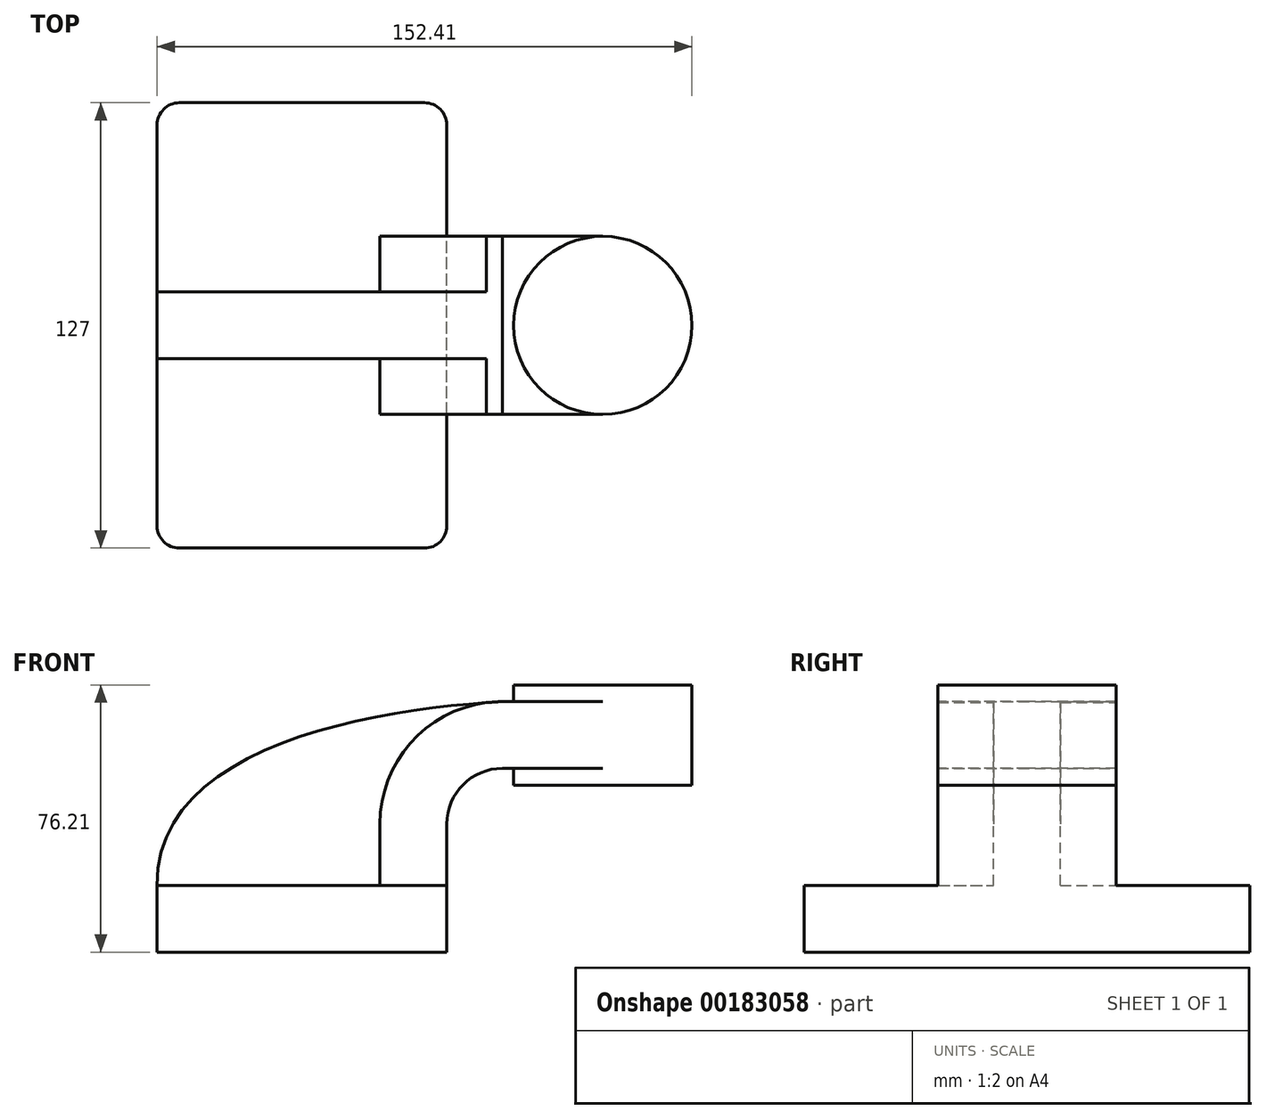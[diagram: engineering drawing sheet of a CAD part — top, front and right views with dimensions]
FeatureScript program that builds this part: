
annotation { "Feature Type Name" : "Feature", "Feature Type Description" : "" }
export const myFeature = defineFeature(function(context is Context, id is Id, definition is map)
    precondition{}
    {
        {
            var Q0;
            Q0=qCreatedBy(makeId("Front.planeOp"),FACE);
            var sketch = newSketch(context, id + "F0", { "sketchPlane" : qUnion([Q0])});
            skLineSegment(sketch, "E0.bottom", {"start": v(-41.28, -9.53) * mm, "end": v(41.28, -9.53) * mm});
            skLineSegment(sketch, "E0.top", {"start": v(-41.28, 9.53) * mm, "end": v(41.28, 9.53) * mm});
            skLineSegment(sketch, "E0.left", {"start": v(-41.28, -9.53) * mm, "end": v(-41.28, 9.53) * mm});
            skLineSegment(sketch, "E0.right", {"start": v(41.28, -9.53) * mm, "end": v(41.28, 9.53) * mm});
            skPoint(sketch, "E0.middle", {"position": v(0, 0) * mm});
            skLineSegment(sketch, "E1.bottom", {"start": v(60.32, 38.1) * mm, "end": v(111.12, 38.1) * mm});
            skLineSegment(sketch, "E1.top", {"start": v(60.32, 66.68) * mm, "end": v(111.12, 66.68) * mm});
            skLineSegment(sketch, "E1.left", {"start": v(60.32, 38.1) * mm, "end": v(60.32, 66.68) * mm});
            skLineSegment(sketch, "E1.right", {"start": v(111.12, 38.1) * mm, "end": v(111.12, 66.68) * mm});
            skPoint(sketch, "E1.middle", {"position": v(85.72, 52.39) * mm});
            skLineSegment(sketch, "E2", {"start": v(41.27, 9.53) * mm, "end": v(41.27, 27) * mm});
            skArc(sketch, "E3", {"start": v(41.27, 27) * mm, "mid": v(45.92, 38.23) * mm, "end": v(57.15, 42.88) * mm});
            skLineSegment(sketch, "E4", {"start": v(57.15, 42.88) * mm, "end": v(85.72, 42.88) * mm});
            skLineSegment(sketch, "E5.0", {"start": v(57.15, 61.93) * mm, "end": v(85.72, 61.93) * mm});
            skArc(sketch, "E5.1", {"start": v(22.22, 27) * mm, "mid": v(32.45, 51.7) * mm, "end": v(57.15, 61.93) * mm});
            skLineSegment(sketch, "E5.2", {"start": v(22.22, 9.53) * mm, "end": v(22.22, 27) * mm});
            skLineSegment(sketch, "E6", {"start": v(85.72, 38.1) * mm, "end": v(85.72, 66.68) * mm});
            skFitSpline(sketch, "E7", {"points": [v(-41.28, 9.52) * mm, v(57.15, 61.93) * mm], "startDerivative": vector(-1.05, 120.28) * mm, "endDerivative": vector(109.9, 6.42) * mm});
            skSolve(sketch);
        }
        {
            var Q0;
            Q0=makeQuery(id+"F0.imprint","IMPRINT",FACE,{"disambiguationData":[TD([[makeQuery(id+"F0.imprint","IMPRINT",EDGE,{"derivedFrom":sQuery(id+"F0.wireOp",EDGE,"E0.bottom")}),1.0]])]});
            extrude(context, id + "F1", {"entities" : qUnion([Q0]), "endBound" : BoundingType.SYMMETRIC, "depth" : 127 * mm});
        }
        {
            var Q0;
            {var subQ1=sQuery(id+"F0.wireOp",EDGE,"E2");Q0=makeQuery(id+"F0.imprint","IMPRINT",FACE,{"disambiguationData":[TD([[makeQuery(id+"F0.imprint","IMPRINT",EDGE,{"derivedFrom":subQ1}),1.0]])]});}
            extrude(context, id + "F2", {"entities" : qUnion([Q0]), "operationType" : NewBodyOperationType.ADD, "endBound" : BoundingType.SYMMETRIC, "depth" : 50.8 * mm});
        }
        {
            var Q0;
            {var subQ0=sQuery(id+"F0.wireOp",EDGE,"E4");var subQ1=sQuery(id+"F0.wireOp",EDGE,"E1.left");var subQ2=makeQuery(id+"F0.imprint","INTERSECT",VERTEX,{"derivedFrom":[subQ1,subQ0]});Q0=makeQuery(id+"F0.imprint","IMPRINT",FACE,{"disambiguationData":[TD([[makeQuery(id+"F0.imprint","IMPRINT",EDGE,{"disambiguationData":[TD([[subQ2,-1.0]])],"derivedFrom":subQ1}),-1.0]])]});}
            extrude(context, id + "F3", {"entities" : qUnion([Q0]), "operationType" : NewBodyOperationType.ADD, "endBound" : BoundingType.SYMMETRIC, "depth" : 50.8 * mm});
        }
        {
            var Q0;
            {var subQ3=sQuery(id+"F0.wireOp",EDGE,"E5.2");Q0=makeQuery(id+"F0.imprint","IMPRINT",FACE,{"disambiguationData":[TD([[makeQuery(id+"F0.imprint","IMPRINT",EDGE,{"derivedFrom":subQ3}),1.0]])]});}
            extrude(context, id + "F4", {"entities" : qUnion([Q0]), "operationType" : NewBodyOperationType.ADD, "endBound" : BoundingType.SYMMETRIC, "depth" : 19.05 * mm});
        }
        {
            var Q0;
            {var subQ0=sQuery(id+"F0.wireOp",EDGE,"E1.right");Q0=makeQuery(id+"F0.imprint","IMPRINT",FACE,{"disambiguationData":[TD([[makeQuery(id+"F0.imprint","IMPRINT",EDGE,{"derivedFrom":subQ0}),1.0]])]});}
            var Q1;
            Q1=sQuery(id+"F0.wireOp",EDGE,"E6");
            revolve(context, id + "F5", {"operationType" : NewBodyOperationType.ADD, "entities" : qUnion([Q0]), "axis" : qUnion([Q1]), "revolveType" : RevolveType.FULL});
        }
        {
            var Q0;
            Q0=makeQuery(id+"F1.opExtrude","CAP_EDGE",EDGE,{"disambiguationData":[OSD([sQuery(id+"F0.wireOp",EDGE,"E0.left")])],"isStart":false});
            var Q1;
            Q1=makeQuery(id+"F1.opExtrude","CAP_EDGE",EDGE,{"disambiguationData":[OSD([sQuery(id+"F0.wireOp",EDGE,"E0.right")])],"isStart":false});
            var Q2;
            Q2=makeQuery(id+"F1.opExtrude","CAP_EDGE",EDGE,{"disambiguationData":[OSD([sQuery(id+"F0.wireOp",EDGE,"E0.right")])],"isStart":true});
            var Q3;
            Q3=makeQuery(id+"F1.opExtrude","CAP_EDGE",EDGE,{"disambiguationData":[OSD([sQuery(id+"F0.wireOp",EDGE,"E0.left")])],"isStart":true});
            fillet(context, id + "F6", {"entities" : qUnion([Q0, Q1, Q2, Q3]), "radius" : 6.35 * mm, "tangentPropagation" : true, "allowEdgeOverflow" : false});
        }
    });
